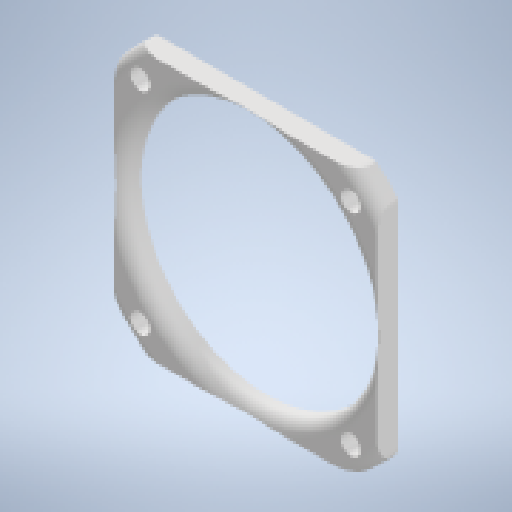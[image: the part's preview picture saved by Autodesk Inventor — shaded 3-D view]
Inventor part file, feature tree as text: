
AUTODESK INVENTOR PART (.ipt)
format: ipt  version: 2023 (Build 270158000, 158)  size: 370,688 bytes
history: native  units: mm
features: sketch x2, revolve x1, extrude x1, fillet x1, chamfer x1
ambient origin geometry x8: Origin, YZ Plane, XZ Plane, XY Plane, X Axis, Y Axis, Z Axis, Center Point
bodies: Solid1 (feature_tree)
feature tree (6):
  revolve  "Revolution1"  [1 undecoded]
  extrude  "Extrusion1"  Depth=3.2mm
  fillet  "Fillet6"  Radius=32.0mm
  chamfer  "Chamfer1"  Distance=3.2mm
  sketch  "Sketch1"  dims[d0=38.0mm d1=40.0mm]
  sketch  "Sketch3"  dims[d2=4.0mm d3=3.2mm d4=32.0mm d5=3.2mm d6=0.0mm d10=3.0mm d13=2.8mm d15=19.0mm d16=5.0mm d17=90.0deg d20=3.2mm d21=2.0mm d22=2.0mm d23=45.0deg d7=0.0mm d8=0.0mm d9=0.0mm]
note: 1 required parameter value undecoded (feature->parameter linkage not recoverable at this tier; creation-order binding heuristic only, values carry confidence <= 0.55)
